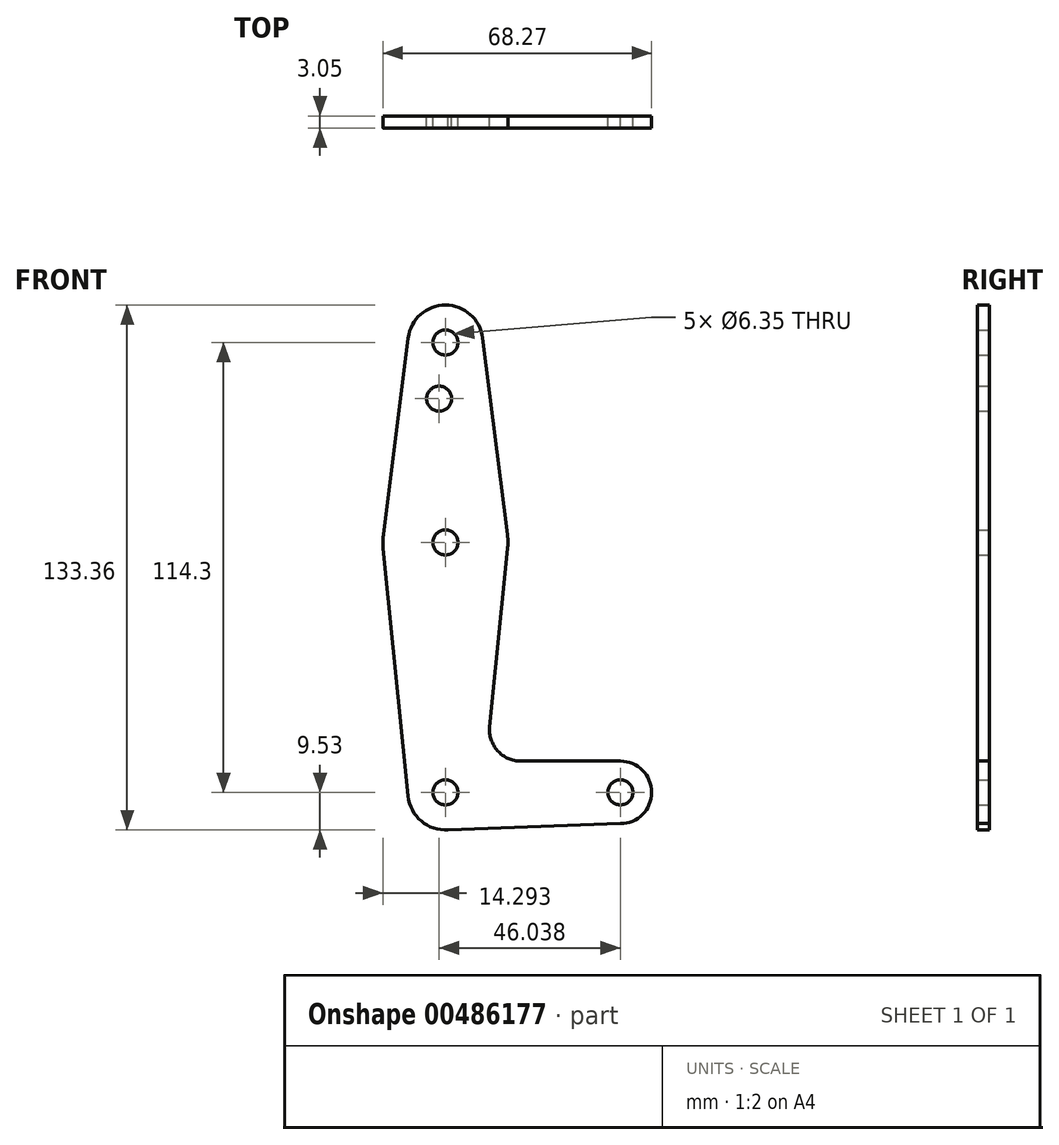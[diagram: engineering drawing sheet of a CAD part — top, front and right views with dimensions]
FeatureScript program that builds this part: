
annotation { "Feature Type Name" : "Feature", "Feature Type Description" : "" }
export const myFeature = defineFeature(function(context is Context, id is Id, definition is map)
    precondition{}
    {
        {
            var Q0;
            Q0=qCreatedBy(makeId("Front.planeOp"),FACE);
            var sketch = newSketch(context, id + "F0", { "sketchPlane" : qUnion([Q0])});
            skLineSegment(sketch, "E0", {"start": v(0, 114.3) * mm, "end": v(0, 0) * mm, "construction": true});
            skLineSegment(sketch, "E1", {"start": v(0, 0) * mm, "end": v(44.45, 0) * mm, "construction": true});
            skCircle(sketch, "E2", {"center": v(0, 63.5) * mm, "radius": 15.88 * mm});
            skCircle(sketch, "E3", {"center": v(0, 114.3) * mm, "radius": 9.53 * mm});
            skCircle(sketch, "E4", {"center": v(0, 0) * mm, "radius": 9.53 * mm});
            skCircle(sketch, "E5", {"center": v(44.45, 0) * mm, "radius": 7.94 * mm});
            skLineSegment(sketch, "E6", {"start": v(9.45, 115.5) * mm, "end": v(15.75, 65.48) * mm});
            skLineSegment(sketch, "E7", {"start": v(-9.45, 115.5) * mm, "end": v(-15.75, 65.48) * mm});
            skLineSegment(sketch, "E8", {"start": v(0, -9.53) * mm, "end": v(44.45, -7.94) * mm});
            skLineSegment(sketch, "E9", {"start": v(19.16, 7.94) * mm, "end": v(44.45, 7.94) * mm});
            skLineSegment(sketch, "E10", {"start": v(-15.8, 61.91) * mm, "end": v(-9.48, -0.95) * mm});
            skLineSegment(sketch, "E11", {"start": v(15.8, 61.91) * mm, "end": v(11.25, 16.68) * mm});
            skArc(sketch, "E12.filletArc", {"start": v(11.25, 16.68) * mm, "mid": v(13.26, 10.55) * mm, "end": v(19.16, 7.94) * mm});
            skCircle(sketch, "E13", {"center": v(0, 114.3) * mm, "radius": 3.18 * mm});
            skCircle(sketch, "E14", {"center": v(-1.59, 100.03) * mm, "radius": 3.18 * mm});
            skCircle(sketch, "E15", {"center": v(0, 63.5) * mm, "radius": 3.18 * mm});
            skCircle(sketch, "E16", {"center": v(0, 0) * mm, "radius": 3.18 * mm});
            skCircle(sketch, "E17", {"center": v(44.45, 0) * mm, "radius": 3.18 * mm});
            skSolve(sketch);
        }
        {
            var Q0;
            Q0 = qSketchRegion(id + "F0", true);
            extrude(context, id + "F1", {"entities" : qUnion([Q0]), "depth" : 3.05 * mm});
        }
    });
